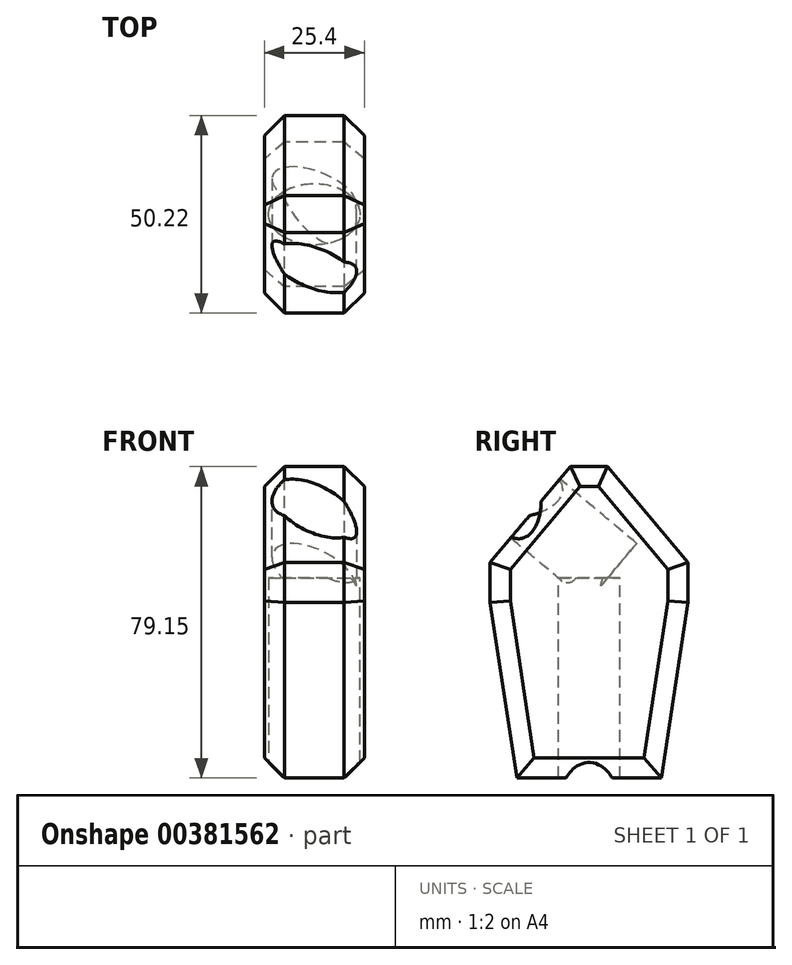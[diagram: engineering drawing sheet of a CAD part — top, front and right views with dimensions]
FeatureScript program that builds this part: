
annotation { "Feature Type Name" : "Feature", "Feature Type Description" : "" }
export const myFeature = defineFeature(function(context is Context, id is Id, definition is map)
    precondition{}
    {
        {
            var Q0;
            Q0=qCreatedBy(makeId("Right.planeOp"),FACE);
            var sketch = newSketch(context, id + "F0", { "sketchPlane" : qUnion([Q0])});
            skLineSegment(sketch, "E0", {"start": v(-25.1, 42.35) * mm, "end": v(-4.7, 66.68) * mm});
            skLineSegment(sketch, "E1", {"start": v(0, 66.68) * mm, "end": v(-4.7, 66.68) * mm});
            skLineSegment(sketch, "E2", {"start": v(-25.1, 42.35) * mm, "end": v(-25.1, 32.14) * mm});
            skLineSegment(sketch, "E3", {"start": v(-25.1, 32.14) * mm, "end": v(-18.36, -12.47) * mm});
            skLineSegment(sketch, "E4", {"start": v(-18.36, -12.47) * mm, "end": v(0, -12.47) * mm});
            skLineSegment(sketch, "E5.MirrorCS", {"start": v(0, 66.68) * mm, "end": v(4.7, 66.68) * mm});
            skLineSegment(sketch, "E6.MirrorCS", {"start": v(25.1, 42.35) * mm, "end": v(4.7, 66.68) * mm});
            skLineSegment(sketch, "E7.MirrorCS", {"start": v(25.1, 42.35) * mm, "end": v(25.1, 32.14) * mm});
            skLineSegment(sketch, "E8.MirrorCS", {"start": v(25.1, 32.14) * mm, "end": v(18.36, -12.47) * mm});
            skLineSegment(sketch, "E9.MirrorCS", {"start": v(18.36, -12.47) * mm, "end": v(0, -12.47) * mm});
            skSolve(sketch);
        }
        {
            var Q0;
            Q0 = qSketchRegion(id + "F0", true);
            extrude(context, id + "F1", {"entities" : qUnion([Q0]), "endBound" : BoundingType.SYMMETRIC, "depth" : 25.4 * mm});
        }
        {
            var Q0;
            Q0=makeQuery(id+"F1.opExtrude","SWEPT_FACE",FACE,{"disambiguationData":[OSD([sQuery(id+"F0.wireOp",EDGE,"E0")])]});
            var sketch = newSketch(context, id + "F2", { "sketchPlane" : qUnion([Q0])});
            skEllipse(sketch, "E10", {"center": v(0, 34.13) * mm, "majorRadius": 12.7 * mm, "minorRadius": 7.08 * mm, "majorAxis": v(0.77, -0.64)});
            skSolve(sketch);
        }
        {
            var Q0;
            Q0 = qSketchRegion(id + "F2", true);
            extrude(context, id + "F3", {"entities" : qUnion([Q0]), "operationType" : NewBodyOperationType.REMOVE, "oppositeDirection" : true, "depth" : 25.4 * mm});
        }
        {
            var Q0;
            Q0=makeQuery(id+"F1.opExtrude","CAP_EDGE",EDGE,{"disambiguationData":[OSD([sQuery(id+"F0.wireOp",EDGE,"E0")])],"isStart":false});
            var Q1;
            Q1=makeQuery(id+"F1.opExtrude","CAP_EDGE",EDGE,{"disambiguationData":[OSD([sQuery(id+"F0.wireOp",EDGE,"E2")])],"isStart":false});
            var Q2;
            Q2=makeQuery(id+"F1.opExtrude","CAP_EDGE",EDGE,{"disambiguationData":[OSD([sQuery(id+"F0.wireOp",EDGE,"E3")])],"isStart":false});
            var Q3;
            Q3=makeQuery(id+"F1.opExtrude","CAP_EDGE",EDGE,{"disambiguationData":[OSD([sQuery(id+"F0.wireOp",EDGE,"E1"),sQuery(id+"F0.wireOp",EDGE,"E5.MirrorCS")])],"isStart":false});
            var Q4;
            Q4=makeQuery(id+"F1.opExtrude","CAP_EDGE",EDGE,{"disambiguationData":[OSD([sQuery(id+"F0.wireOp",EDGE,"E6.MirrorCS")])],"isStart":false});
            var Q5;
            Q5=makeQuery(id+"F1.opExtrude","CAP_EDGE",EDGE,{"disambiguationData":[OSD([sQuery(id+"F0.wireOp",EDGE,"E7.MirrorCS")])],"isStart":false});
            var Q6;
            Q6=makeQuery(id+"F1.opExtrude","CAP_EDGE",EDGE,{"disambiguationData":[OSD([sQuery(id+"F0.wireOp",EDGE,"E8.MirrorCS")])],"isStart":false});
            var Q7;
            Q7=makeQuery(id+"F1.opExtrude","CAP_EDGE",EDGE,{"disambiguationData":[OSD([sQuery(id+"F0.wireOp",EDGE,"E4"),sQuery(id+"F0.wireOp",EDGE,"E9.MirrorCS")])],"isStart":false});
            var Q8;
            Q8=makeQuery(id+"F1.opExtrude","CAP_EDGE",EDGE,{"disambiguationData":[OSD([sQuery(id+"F0.wireOp",EDGE,"E7.MirrorCS")])],"isStart":true});
            var Q9;
            Q9=makeQuery(id+"F1.opExtrude","CAP_EDGE",EDGE,{"disambiguationData":[OSD([sQuery(id+"F0.wireOp",EDGE,"E2")])],"isStart":true});
            var Q10;
            Q10=makeQuery(id+"F1.opExtrude","CAP_EDGE",EDGE,{"disambiguationData":[OSD([sQuery(id+"F0.wireOp",EDGE,"E1"),sQuery(id+"F0.wireOp",EDGE,"E5.MirrorCS")])],"isStart":true});
            var Q11;
            Q11=makeQuery(id+"F1.opExtrude","CAP_EDGE",EDGE,{"disambiguationData":[OSD([sQuery(id+"F0.wireOp",EDGE,"E0")])],"isStart":true});
            var Q12;
            Q12=makeQuery(id+"F1.opExtrude","CAP_FACE",FACE,{"disambiguationData":[OSD([sQuery(id+"F0.wireOp",EDGE,"E0"),sQuery(id+"F0.wireOp",EDGE,"E1"),sQuery(id+"F0.wireOp",EDGE,"E2"),sQuery(id+"F0.wireOp",EDGE,"E3"),sQuery(id+"F0.wireOp",EDGE,"E4"),sQuery(id+"F0.wireOp",EDGE,"E5.MirrorCS"),sQuery(id+"F0.wireOp",EDGE,"E6.MirrorCS"),sQuery(id+"F0.wireOp",EDGE,"E7.MirrorCS"),sQuery(id+"F0.wireOp",EDGE,"E8.MirrorCS"),sQuery(id+"F0.wireOp",EDGE,"E9.MirrorCS")])],"isStart":true});
            chamfer(context, id + "F4", {"entities" : qUnion([Q0, Q1, Q2, Q3, Q4, Q5, Q6, Q7, Q8, Q9, Q10, Q11, Q12]), "width" : 5.08 * mm, "tangentPropagation" : true});
        }
        {
            var Q0;
            Q0=makeQuery(id+"F1.opExtrude","SWEPT_FACE",FACE,{"disambiguationData":[OSD([sQuery(id+"F0.wireOp",EDGE,"E4"),sQuery(id+"F0.wireOp",EDGE,"E9.MirrorCS")])]});
            var sketch = newSketch(context, id + "F5", { "sketchPlane" : qUnion([Q0])});
            skEllipse(sketch, "E11", {"center": v(0, 0) * mm, "majorRadius": 11.6 * mm, "minorRadius": 7.8 * mm, "majorAxis": v(-1, 0)});
            skSolve(sketch);
        }
        {
            var Q0;
            {var subQ0=sQuery(id+"F5.wireOp",EDGE,"E11");var subQ1=sQuery(id+"F0.wireOp",EDGE,"E9.MirrorCS");var subQ2=sQuery(id+"F0.wireOp",EDGE,"E4");var subQ3=makeQuery(id+"F4.opChamfer","BLEND_EDGE",EDGE,{"blendedFrom":[makeQuery(id+"F1.opExtrude","CAP_EDGE",EDGE,{"disambiguationData":[OSD([subQ2,subQ1])],"isStart":false}),makeQuery(id+"F1.opExtrude","SWEPT_FACE",FACE,{"disambiguationData":[OSD([subQ2,subQ1])]})],"blendedInto":[makeQuery(id+"F1.opExtrude","SWEPT_FACE",FACE,{"disambiguationData":[OSD([subQ2,subQ1])]})]});var subQ4=makeQuery(id+"F5.imprint","INTERSECT",VERTEX,{"disambiguationData":[OD(0.0)],"derivedFrom":[subQ3,subQ0]});Q0=makeQuery(id+"F5.imprint","IMPRINT",FACE,{"disambiguationData":[TD([[makeQuery(id+"F5.imprint","IMPRINT",EDGE,{"disambiguationData":[TD([[subQ4,-1.0]])],"derivedFrom":subQ0}),1.0]])]});}
            var Q1;
            {var subQ0=sQuery(id+"F5.wireOp",EDGE,"E11");var subQ1=sQuery(id+"F0.wireOp",EDGE,"E9.MirrorCS");var subQ2=sQuery(id+"F0.wireOp",EDGE,"E4");var subQ3=makeQuery(id+"F4.opChamfer","BLEND_EDGE",EDGE,{"blendedFrom":[makeQuery(id+"F1.opExtrude","CAP_EDGE",EDGE,{"disambiguationData":[OSD([subQ2,subQ1])],"isStart":true}),makeQuery(id+"F1.opExtrude","SWEPT_FACE",FACE,{"disambiguationData":[OSD([subQ2,subQ1])]})],"blendedInto":[makeQuery(id+"F1.opExtrude","SWEPT_FACE",FACE,{"disambiguationData":[OSD([subQ2,subQ1])]})]});var subQ4=makeQuery(id+"F5.imprint","INTERSECT",VERTEX,{"disambiguationData":[OD(0.0)],"derivedFrom":[subQ3,subQ0]});Q1=makeQuery(id+"F5.imprint","IMPRINT",FACE,{"disambiguationData":[TD([[makeQuery(id+"F5.imprint","IMPRINT",EDGE,{"disambiguationData":[TD([[subQ4,1.0]])],"derivedFrom":subQ0}),1.0]])]});}
            var Q2;
            {var subQ0=sQuery(id+"F5.wireOp",EDGE,"E11");var subQ1=sQuery(id+"F0.wireOp",EDGE,"E9.MirrorCS");var subQ2=sQuery(id+"F0.wireOp",EDGE,"E4");var subQ3=makeQuery(id+"F1.opExtrude","SWEPT_FACE",FACE,{"disambiguationData":[OSD([subQ2,subQ1])]});var subQ4=makeQuery(id+"F4.opChamfer","BLEND_EDGE",EDGE,{"blendedFrom":[makeQuery(id+"F1.opExtrude","CAP_EDGE",EDGE,{"disambiguationData":[OSD([subQ2,subQ1])],"isStart":false}),subQ3],"blendedInto":[subQ3]});var subQ5=makeQuery(id+"F5.imprint","INTERSECT",VERTEX,{"disambiguationData":[OD(0.0)],"derivedFrom":[subQ4,subQ0]});Q2=makeQuery(id+"F5.imprint","IMPRINT",FACE,{"disambiguationData":[TD([[makeQuery(id+"F5.imprint","IMPRINT",EDGE,{"disambiguationData":[TD([[subQ5,1.0]])],"derivedFrom":subQ0}),1.0]])]});}
            extrude(context, id + "F6", {"entities" : qUnion([Q0, Q1, Q2]), "operationType" : NewBodyOperationType.REMOVE, "oppositeDirection" : true, "depth" : 50.8 * mm});
        }
    });
